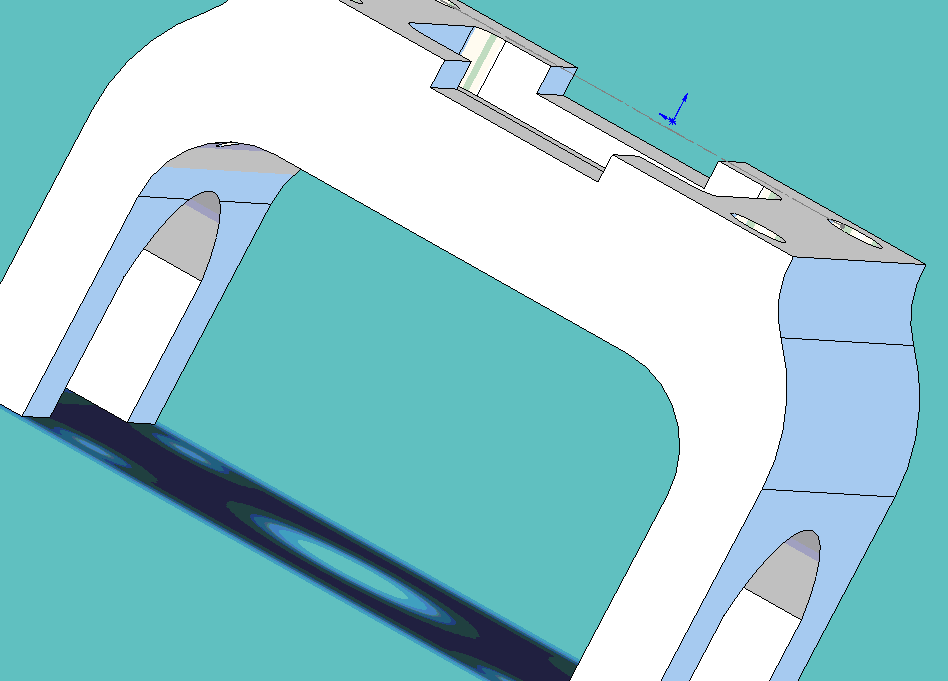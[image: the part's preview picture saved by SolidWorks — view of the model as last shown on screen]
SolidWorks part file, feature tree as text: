
SOLIDWORKS PART (.sldprt)
format: sldprt  version: not decoded by parser v0  size: 395,776 bytes
history: native  units: mm
features: sketch x6, cut_extrude x4, plane x3, fillet x2, material x1, extrude x1, pattern_linear x1 (+10 scaffold rows collapsed)
feature tree (28):
  scaffold x10  (default folders/planes/origin — collapsed)
  material  "Material <not specified>"
  plane  "Frontal"
  plane  "Horizontal"
  plane  "Profile"
  sketch  "Sketch1"  dims[c1.D5=~6.092013mm c1.D1=12.7mm c1.D2=25.4mm c2.D5=12.7mm c2.D9=12.7mm c2.D1=26.035mm c2.D2=3.81mm c2.D3=24.13mm c3.D1=26.035mm c3.D4=26.035mm c3.D5=20.32mm c3.D6=10.16mm c3.D7=36.83mm c3.D8=30.48mm c3.D9=20.32mm c3.D10=3.81mm c3.D11=12.065mm]
  extrude  "Extrude1"  Depth=60.96mm
  sketch  "Sketch4"  dims[D1=19.05mm D2=19.558mm D3=12.7mm D4=35.56mm]
  cut_extrude  "Cut-Extrude1"  [1 undecoded]
  sketch  "Sketch5"  dims[D1=16.002mm D2=16.002mm D3=12.192mm D4=12.192mm]
  cut_extrude  "Cut-Extrude3"  Depth=3.81mm
  fillet  "Fillet1"  Radius=3.556mm
  fillet  "Fillet2"  Radius=3.556mm
  sketch  "Sketch6"  dims[D1=24.13mm D2=18.288mm D3=38.1mm]
  cut_extrude  "Cut-Extrude4"  [1 undecoded]
  sketch  "Sketch7"  dims[D3=~3.510979mm D1=8.255mm D2=7.62mm]
  cut_extrude  "Cut-Extrude5"  [1 undecoded]
  sketch  "Sketch8"
  pattern_linear  "LPattern1"  Count1=2 Count2=2 Spacing1=60.96mm Spacing2=44.45mm
decode coverage: 10 of 14 modeling features carry decoded parameters
note: ~ marks probable driven/reference dimensions
note: 3 parameter values undecoded
summary: no parameter record found for 3 features
note: suppression state not decoded; provenance and decode notes live in map.json
